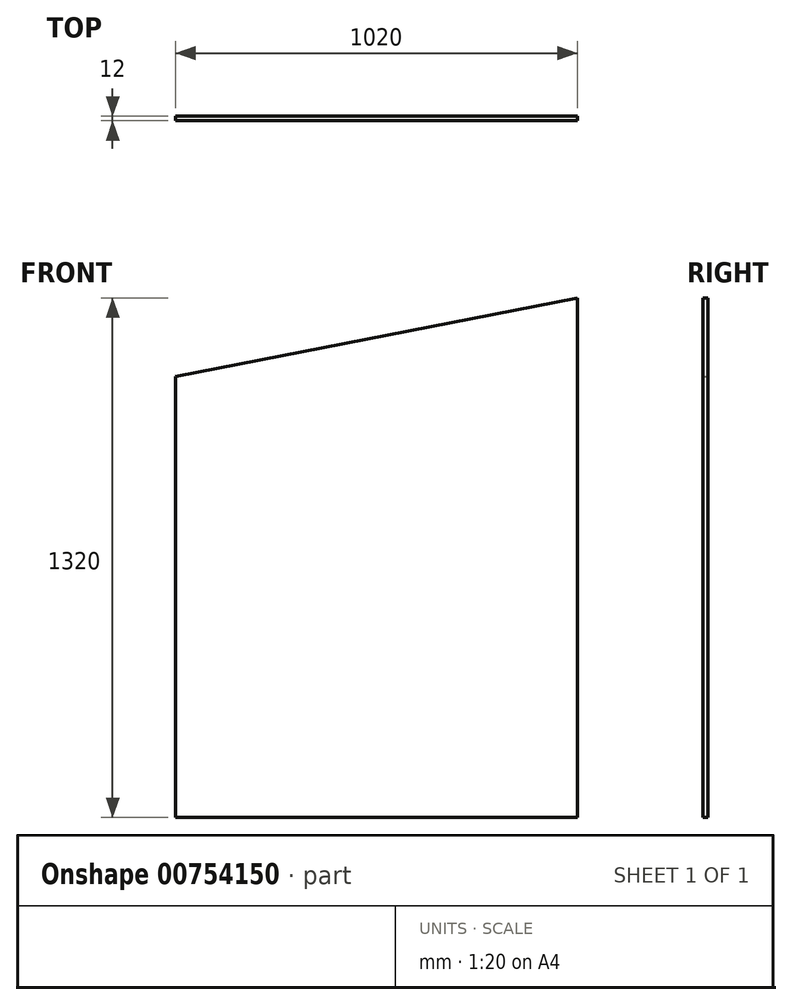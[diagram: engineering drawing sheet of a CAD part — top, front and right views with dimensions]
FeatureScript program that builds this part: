
annotation { "Feature Type Name" : "Feature", "Feature Type Description" : "" }
export const myFeature = defineFeature(function(context is Context, id is Id, definition is map)
    precondition{}
    {
        {
            var Q0;
            Q0=qCreatedBy(makeId("Front.planeOp"),FACE);
            var sketch = newSketch(context, id + "F0", { "sketchPlane" : qUnion([Q0])});
            skLineSegment(sketch, "E0", {"start": v(0, 0) * mm, "end": v(1020, 0) * mm});
            skLineSegment(sketch, "E1", {"start": v(1020, 0) * mm, "end": v(1020, 1320) * mm});
            skLineSegment(sketch, "E2", {"start": v(1020, 1320) * mm, "end": v(0, 1120) * mm});
            skLineSegment(sketch, "E3", {"start": v(0, 1120) * mm, "end": v(0, 0) * mm});
            skSolve(sketch);
        }
        {
            var Q0;
            Q0 = qSketchRegion(id + "F0", true);
            extrude(context, id + "F1", {"entities" : qUnion([Q0]), "depth" : 12 * mm, "offsetDistance" : 25 * mm});
        }
    });
